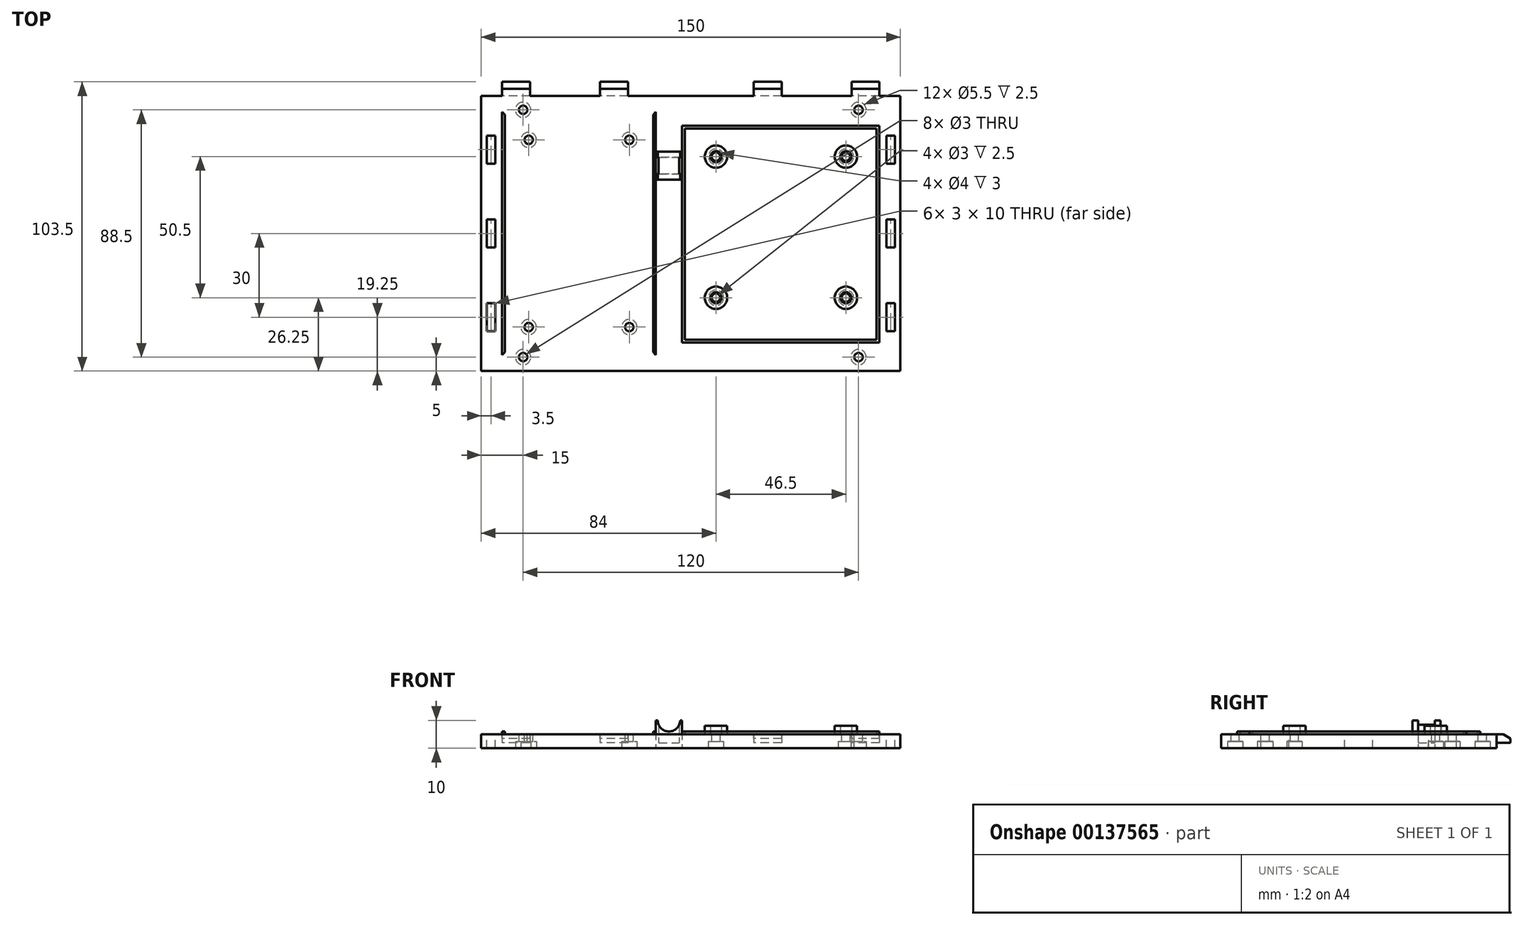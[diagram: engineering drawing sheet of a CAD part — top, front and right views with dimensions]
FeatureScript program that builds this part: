
annotation { "Feature Type Name" : "Feature", "Feature Type Description" : "" }
export const myFeature = defineFeature(function(context is Context, id is Id, definition is map)
    precondition{}
    {
        {
            var Q0;
            Q0=qCreatedBy(makeId("Top.planeOp"),FACE);
            var sketch = newSketch(context, id + "F0", { "sketchPlane" : qUnion([Q0])});
            skLineSegment(sketch, "E0.bottom", {"start": v(75, 49.25) * mm, "end": v(-75, 49.25) * mm});
            skLineSegment(sketch, "E0.top", {"start": v(75, -49.25) * mm, "end": v(-75, -49.25) * mm});
            skLineSegment(sketch, "E0.left", {"start": v(75, 49.25) * mm, "end": v(75, -49.25) * mm});
            skLineSegment(sketch, "E0.right", {"start": v(-75, 49.25) * mm, "end": v(-75, -49.25) * mm});
            skPoint(sketch, "E0.middle", {"position": v(0, 0) * mm});
            skSolve(sketch);
        }
        {
            var Q0;
            Q0=makeQuery(id+"F0.imprint","IMPRINT",FACE,{"disambiguationData":[TD([[makeQuery(id+"F0.imprint","IMPRINT",EDGE,{"derivedFrom":sQuery(id+"F0.wireOp",EDGE,"E0.bottom")}),1.0]])]});
            extrude(context, id + "F1", {"entities" : qUnion([Q0]), "depth" : 5 * mm});
        }
        {
            var Q0;
            Q0=makeQuery(id+"F1.opExtrude","CAP_FACE",FACE,{"disambiguationData":[OSD([sQuery(id+"F0.wireOp",EDGE,"E0.bottom"),sQuery(id+"F0.wireOp",EDGE,"E0.top"),sQuery(id+"F0.wireOp",EDGE,"E0.left"),sQuery(id+"F0.wireOp",EDGE,"E0.right")])],"isStart":false});
            var sketch = newSketch(context, id + "F2", { "sketchPlane" : qUnion([Q0])});
            skLineSegment(sketch, "E1.bottom", {"start": v(-62.5, 38.5) * mm, "end": v(-17.5, 38.5) * mm});
            skLineSegment(sketch, "E1.top", {"start": v(-62.5, -38.5) * mm, "end": v(-17.5, -38.5) * mm});
            skLineSegment(sketch, "E1.left", {"start": v(-62.5, 38.5) * mm, "end": v(-62.5, -38.5) * mm});
            skLineSegment(sketch, "E1.right", {"start": v(-17.5, 38.5) * mm, "end": v(-17.5, -38.5) * mm});
            skLineSegment(sketch, "E2.bottom", {"start": v(1.85, 33.5) * mm, "end": v(62.5, 33.5) * mm});
            skLineSegment(sketch, "E2.top", {"start": v(1.85, -34.05) * mm, "end": v(62.5, -34.05) * mm});
            skLineSegment(sketch, "E2.left", {"start": v(1.85, 33.5) * mm, "end": v(1.85, -34.05) * mm});
            skLineSegment(sketch, "E2.right", {"start": v(62.5, 33.5) * mm, "end": v(62.5, -34.05) * mm});
            skSolve(sketch);
        }
        {
            var Q0;
            Q0=makeQuery(id+"F2.imprint","IMPRINT",FACE,{"disambiguationData":[TD([[makeQuery(id+"F2.imprint","IMPRINT",EDGE,{"derivedFrom":sQuery(id+"F2.wireOp",EDGE,"E1.bottom")}),1.0]])]});
            var sketch = newSketch(context, id + "F3", { "sketchPlane" : qUnion([Q0])});
            skLineSegment(sketch, "E3.left", {"start": v(-66.5, 42.5) * mm, "end": v(-66.5, -42.5) * mm});
            skLineSegment(sketch, "E3.right", {"start": v(-13.5, 42.5) * mm, "end": v(-13.5, -42.5) * mm});
            skLineSegment(sketch, "E4.bottom", {"start": v(-2.15, 37.5) * mm, "end": v(66.5, 37.5) * mm});
            skLineSegment(sketch, "E4.top", {"start": v(-2.15, -38.05) * mm, "end": v(66.5, -38.05) * mm});
            skLineSegment(sketch, "E4.left", {"start": v(-2.15, 37.5) * mm, "end": v(-2.15, -38.05) * mm});
            skLineSegment(sketch, "E4.right", {"start": v(66.5, 37.5) * mm, "end": v(66.5, -38.05) * mm});
            skLineSegment(sketch, "E5.left", {"start": v(-67.5, 43.5) * mm, "end": v(-67.5, -43.5) * mm});
            skLineSegment(sketch, "E5.right", {"start": v(-12.5, 43.5) * mm, "end": v(-12.5, -43.5) * mm});
            skLineSegment(sketch, "E6.bottom", {"start": v(-3.15, 38.5) * mm, "end": v(67.5, 38.5) * mm});
            skLineSegment(sketch, "E6.top", {"start": v(-3.15, -39.05) * mm, "end": v(67.5, -39.05) * mm});
            skLineSegment(sketch, "E6.left", {"start": v(-3.15, 38.5) * mm, "end": v(-3.15, -39.05) * mm});
            skLineSegment(sketch, "E6.right", {"start": v(67.5, 38.5) * mm, "end": v(67.5, -39.05) * mm});
            skLineSegment(sketch, "E7", {"start": v(-67.5, 43.5) * mm, "end": v(-66.5, 42.5) * mm});
            skLineSegment(sketch, "E8", {"start": v(-12.5, 43.5) * mm, "end": v(-13.5, 42.5) * mm});
            skLineSegment(sketch, "E9", {"start": v(-12.5, -43.5) * mm, "end": v(-13.5, -42.5) * mm});
            skLineSegment(sketch, "E10", {"start": v(-67.5, -43.5) * mm, "end": v(-66.5, -42.5) * mm});
            skSolve(sketch);
        }
        {
            var Q0;
            Q0 = qSketchRegion(id + "F3", true);
            extrude(context, id + "F4", {"entities" : qUnion([Q0]), "operationType" : NewBodyOperationType.ADD, "depth" : 1 * mm});
        }
        {
            var Q0;
            Q0=makeQuery(id+"F2.imprint","IMPRINT",FACE,{"disambiguationData":[TD([[makeQuery(id+"F2.imprint","IMPRINT",EDGE,{"derivedFrom":sQuery(id+"F2.wireOp",EDGE,"E1.bottom")}),1.0]])]});
            var sketch = newSketch(context, id + "F5", { "sketchPlane" : qUnion([Q0])});
            skCircle(sketch, "E11", {"center": v(9, 27.5) * mm, "radius": 2 * mm});
            skCircle(sketch, "E12", {"center": v(55.5, 27.5) * mm, "radius": 2 * mm});
            skCircle(sketch, "E13", {"center": v(9, -23) * mm, "radius": 2 * mm});
            skCircle(sketch, "E14", {"center": v(55.5, -23) * mm, "radius": 2 * mm});
            skCircle(sketch, "E15", {"center": v(9, 27.5) * mm, "radius": 4 * mm});
            skCircle(sketch, "E16", {"center": v(55.5, 27.5) * mm, "radius": 4 * mm});
            skCircle(sketch, "E17", {"center": v(55.5, -23) * mm, "radius": 4 * mm});
            skCircle(sketch, "E18", {"center": v(9, -23) * mm, "radius": 4 * mm});
            skSolve(sketch);
        }
        {
            var Q0;
            Q0 = qSketchRegion(id + "F5", true);
            extrude(context, id + "F6", {"entities" : qUnion([Q0]), "operationType" : NewBodyOperationType.ADD, "depth" : 3 * mm});
        }
        {
            var Q0;
            Q0=makeQuery(id+"F2.imprint","IMPRINT",FACE,{"disambiguationData":[TD([[makeQuery(id+"F2.imprint","IMPRINT",EDGE,{"derivedFrom":sQuery(id+"F2.wireOp",EDGE,"E2.bottom")}),-1.0]])]});
            var sketch = newSketch(context, id + "F7", { "sketchPlane" : qUnion([Q0])});
            skCircle(sketch, "E19", {"center": v(9, 27.5) * mm, "radius": 1.5 * mm});
            skCircle(sketch, "E20", {"center": v(55.5, 27.5) * mm, "radius": 1.5 * mm});
            skCircle(sketch, "E21", {"center": v(9, -23) * mm, "radius": 1.5 * mm});
            skCircle(sketch, "E22", {"center": v(55.5, -23) * mm, "radius": 1.5 * mm});
            skCircle(sketch, "E23", {"center": v(-58, 33.5) * mm, "radius": 1.5 * mm});
            skCircle(sketch, "E24", {"center": v(-22, 33.5) * mm, "radius": 1.5 * mm});
            skCircle(sketch, "E25", {"center": v(-58, -33.5) * mm, "radius": 1.5 * mm});
            skCircle(sketch, "E26", {"center": v(-22, -33.5) * mm, "radius": 1.5 * mm});
            skCircle(sketch, "E27", {"center": v(-60, -44.25) * mm, "radius": 1.5 * mm});
            skCircle(sketch, "E28", {"center": v(60, -44.25) * mm, "radius": 1.5 * mm});
            skCircle(sketch, "E29", {"center": v(60, 44.25) * mm, "radius": 1.5 * mm});
            skCircle(sketch, "E30", {"center": v(-60, 44.25) * mm, "radius": 1.5 * mm});
            skSolve(sketch);
        }
        {
            var Q0;
            Q0 = qSketchRegion(id + "F7", true);
            extrude(context, id + "F8", {"entities" : qUnion([Q0]), "operationType" : NewBodyOperationType.REMOVE, "endBound" : BoundingType.SYMMETRIC, "oppositeDirection" : true, "depth" : 25 * mm});
        }
        {
            var Q0;
            Q0=makeQuery(id+"F1.opExtrude","CAP_FACE",FACE,{"disambiguationData":[OSD([sQuery(id+"F0.wireOp",EDGE,"E0.bottom"),sQuery(id+"F0.wireOp",EDGE,"E0.top"),sQuery(id+"F0.wireOp",EDGE,"E0.left"),sQuery(id+"F0.wireOp",EDGE,"E0.right")])],"isStart":true});
            var sketch = newSketch(context, id + "F9", { "sketchPlane" : qUnion([Q0])});
            skCircle(sketch, "E31", {"center": v(9, 23) * mm, "radius": 2.75 * mm});
            skCircle(sketch, "E32", {"center": v(55.5, 23) * mm, "radius": 2.75 * mm});
            skCircle(sketch, "E33", {"center": v(9, -27.5) * mm, "radius": 2.75 * mm});
            skCircle(sketch, "E34", {"center": v(55.5, -27.5) * mm, "radius": 2.75 * mm});
            skCircle(sketch, "E35", {"center": v(-22, -33.5) * mm, "radius": 2.75 * mm});
            skCircle(sketch, "E36", {"center": v(-58, -33.5) * mm, "radius": 2.75 * mm});
            skCircle(sketch, "E37", {"center": v(-22, 33.5) * mm, "radius": 2.75 * mm});
            skCircle(sketch, "E38", {"center": v(-58, 33.5) * mm, "radius": 2.75 * mm});
            skCircle(sketch, "E39", {"center": v(-60, -44.25) * mm, "radius": 2.75 * mm});
            skCircle(sketch, "E40", {"center": v(60, -44.25) * mm, "radius": 2.75 * mm});
            skCircle(sketch, "E41", {"center": v(-60, 44.25) * mm, "radius": 2.75 * mm});
            skCircle(sketch, "E42", {"center": v(60, 44.25) * mm, "radius": 2.75 * mm});
            skSolve(sketch);
        }
        {
            var Q0;
            Q0 = qSketchRegion(id + "F9", true);
            extrude(context, id + "F10", {"entities" : qUnion([Q0]), "operationType" : NewBodyOperationType.REMOVE, "oppositeDirection" : true, "depth" : 2.5 * mm});
        }
        {
            var Q0;
            Q0=makeQuery(id+"F2.imprint","IMPRINT",FACE,{"disambiguationData":[TD([[makeQuery(id+"F2.imprint","IMPRINT",EDGE,{"derivedFrom":sQuery(id+"F2.wireOp",EDGE,"E1.bottom")}),1.0]])]});
            var sketch = newSketch(context, id + "F11", { "sketchPlane" : qUnion([Q0])});
            skLineSegment(sketch, "E43.bottom", {"start": v(-73, 35) * mm, "end": v(-70, 35) * mm});
            skLineSegment(sketch, "E43.top", {"start": v(-73, 25) * mm, "end": v(-70, 25) * mm});
            skLineSegment(sketch, "E43.left", {"start": v(-73, 35) * mm, "end": v(-73, 25) * mm});
            skLineSegment(sketch, "E43.right", {"start": v(-70, 35) * mm, "end": v(-70, 25) * mm});
            skLineSegment(sketch, "E44.bottom", {"start": v(-73, 5) * mm, "end": v(-70, 5) * mm});
            skLineSegment(sketch, "E44.top", {"start": v(-73, -5) * mm, "end": v(-70, -5) * mm});
            skLineSegment(sketch, "E44.left", {"start": v(-73, 5) * mm, "end": v(-73, -5) * mm});
            skLineSegment(sketch, "E44.right", {"start": v(-70, 5) * mm, "end": v(-70, -5) * mm});
            skLineSegment(sketch, "E45.bottom", {"start": v(-73, -25) * mm, "end": v(-70, -25) * mm});
            skLineSegment(sketch, "E45.top", {"start": v(-73, -35) * mm, "end": v(-70, -35) * mm});
            skLineSegment(sketch, "E45.left", {"start": v(-73, -25) * mm, "end": v(-73, -35) * mm});
            skLineSegment(sketch, "E45.right", {"start": v(-70, -25) * mm, "end": v(-70, -35) * mm});
            skLineSegment(sketch, "E46.MirrorCS", {"start": v(73, -35) * mm, "end": v(70, -35) * mm});
            skLineSegment(sketch, "E47.MirrorCS", {"start": v(73, 35) * mm, "end": v(70, 35) * mm});
            skLineSegment(sketch, "E48.MirrorCS", {"start": v(73, -25) * mm, "end": v(70, -25) * mm});
            skLineSegment(sketch, "E49.MirrorCS", {"start": v(73, 25) * mm, "end": v(70, 25) * mm});
            skLineSegment(sketch, "E50.MirrorCS", {"start": v(73, 5) * mm, "end": v(70, 5) * mm});
            skLineSegment(sketch, "E51.MirrorCS", {"start": v(73, -5) * mm, "end": v(70, -5) * mm});
            skLineSegment(sketch, "E52.MirrorCS", {"start": v(70, -25) * mm, "end": v(70, -35) * mm});
            skLineSegment(sketch, "E53.MirrorCS", {"start": v(73, -25) * mm, "end": v(73, -35) * mm});
            skLineSegment(sketch, "E54.MirrorCS", {"start": v(73, 35) * mm, "end": v(73, 25) * mm});
            skLineSegment(sketch, "E55.MirrorCS", {"start": v(70, 35) * mm, "end": v(70, 25) * mm});
            skLineSegment(sketch, "E56.MirrorCS", {"start": v(73, 5) * mm, "end": v(73, -5) * mm});
            skLineSegment(sketch, "E57.MirrorCS", {"start": v(70, 5) * mm, "end": v(70, -5) * mm});
            skSolve(sketch);
        }
        {
            var Q0;
            Q0 = qSketchRegion(id + "F11", true);
            extrude(context, id + "F12", {"entities" : qUnion([Q0]), "operationType" : NewBodyOperationType.REMOVE, "oppositeDirection" : true, "depth" : 25 * mm});
        }
        {
            var Q0;
            Q0=makeQuery(id+"F2.imprint","IMPRINT",FACE,{"disambiguationData":[TD([[makeQuery(id+"F2.imprint","IMPRINT",EDGE,{"derivedFrom":sQuery(id+"F2.wireOp",EDGE,"E1.bottom")}),1.0]])]});
            var sketch = newSketch(context, id + "F13", { "sketchPlane" : qUnion([Q0])});
            skLineSegment(sketch, "E58.bottom", {"start": v(-12.5, 29.25) * mm, "end": v(-3.15, 29.25) * mm});
            skLineSegment(sketch, "E58.top", {"start": v(-12.5, 19.25) * mm, "end": v(-3.15, 19.25) * mm});
            skLineSegment(sketch, "E58.left", {"start": v(-12.5, 29.25) * mm, "end": v(-12.5, 19.25) * mm});
            skLineSegment(sketch, "E58.right", {"start": v(-3.15, 29.25) * mm, "end": v(-3.15, 19.25) * mm});
            skLineSegment(sketch, "E59.bottom", {"start": v(-12.5, 27.25) * mm, "end": v(-11.5, 27.25) * mm});
            skLineSegment(sketch, "E59.top", {"start": v(-12.5, 21.25) * mm, "end": v(-11.5, 21.25) * mm});
            skLineSegment(sketch, "E59.left", {"start": v(-12.5, 27.25) * mm, "end": v(-12.5, 21.25) * mm});
            skLineSegment(sketch, "E59.right", {"start": v(-11.5, 27.25) * mm, "end": v(-11.5, 21.25) * mm});
            skLineSegment(sketch, "E60", {"start": v(-7.82, 29.25) * mm, "end": v(-7.82, 19.25) * mm});
            skLineSegment(sketch, "E61.MirrorCS", {"start": v(-4.15, 27.25) * mm, "end": v(-4.15, 21.25) * mm});
            skLineSegment(sketch, "E62.MirrorCS", {"start": v(-3.15, 27.25) * mm, "end": v(-3.15, 21.25) * mm});
            skLineSegment(sketch, "E63.MirrorCS", {"start": v(-3.15, 21.25) * mm, "end": v(-4.15, 21.25) * mm});
            skLineSegment(sketch, "E64.MirrorCS", {"start": v(-3.15, 27.25) * mm, "end": v(-4.15, 27.25) * mm});
            skSolve(sketch);
        }
        {
            var Q0;
            {var subQ4=sQuery(id+"F13.wireOp",EDGE,"E59.bottom");Q0=makeQuery(id+"F13.imprint","IMPRINT",FACE,{"disambiguationData":[TD([[makeQuery(id+"F13.imprint","IMPRINT",EDGE,{"derivedFrom":subQ4}),1.0]])]});}
            var Q1;
            {var subQ0=sQuery(id+"F13.wireOp",EDGE,"E60");Q1=makeQuery(id+"F13.imprint","IMPRINT",FACE,{"disambiguationData":[TD([[makeQuery(id+"F13.imprint","IMPRINT",EDGE,{"derivedFrom":subQ0}),1.0]])]});}
            extrude(context, id + "F14", {"entities" : qUnion([Q0, Q1]), "operationType" : NewBodyOperationType.ADD, "depth" : 5 * mm});
        }
        {
            var Q0;
            Q0=makeQuery(id+"F14.opExtrude","SWEPT_FACE",FACE,{"disambiguationData":[OSD([sQuery(id+"F13.wireOp",EDGE,"E58.top")])]});
            var sketch = newSketch(context, id + "F15", { "sketchPlane" : qUnion([Q0])});
            skCircle(sketch, "E65", {"center": v(-7.82, 10) * mm, "radius": 4 * mm});
            skSolve(sketch);
        }
        {
            var Q0;
            Q0 = qSketchRegion(id + "F15", true);
            extrude(context, id + "F16", {"entities" : qUnion([Q0]), "operationType" : NewBodyOperationType.REMOVE, "oppositeDirection" : true, "depth" : 25 * mm});
        }
        {
            var Q0;
            Q0=makeQuery(id+"F13.imprint","IMPRINT",FACE,{"disambiguationData":[TD([[makeQuery(id+"F13.imprint","IMPRINT",EDGE,{"derivedFrom":sQuery(id+"F13.wireOp",EDGE,"E59.bottom")}),-1.0]])]});
            var Q1;
            Q1=makeQuery(id+"F13.imprint","IMPRINT",FACE,{"disambiguationData":[TD([[makeQuery(id+"F13.imprint","IMPRINT",EDGE,{"derivedFrom":sQuery(id+"F13.wireOp",EDGE,"E61.MirrorCS")}),1.0]])]});
            extrude(context, id + "F17", {"entities" : qUnion([Q0, Q1]), "operationType" : NewBodyOperationType.REMOVE, "oppositeDirection" : true, "depth" : 25 * mm});
        }
        {
            var Q0;
            Q0=makeQuery(id+"F1.opExtrude","CAP_FACE",FACE,{"disambiguationData":[OSD([sQuery(id+"F0.wireOp",EDGE,"E0.bottom"),sQuery(id+"F0.wireOp",EDGE,"E0.top"),sQuery(id+"F0.wireOp",EDGE,"E0.left"),sQuery(id+"F0.wireOp",EDGE,"E0.right")])],"isStart":true});
            var sketch = newSketch(context, id + "F18", { "sketchPlane" : qUnion([Q0])});
            skLineSegment(sketch, "E66.bottom", {"start": v(-12.5, -27.25) * mm, "end": v(-3.15, -27.25) * mm});
            skLineSegment(sketch, "E66.top", {"start": v(-12.5, -21.25) * mm, "end": v(-3.15, -21.25) * mm});
            skLineSegment(sketch, "E66.left", {"start": v(-12.5, -27.25) * mm, "end": v(-12.5, -21.25) * mm});
            skLineSegment(sketch, "E66.right", {"start": v(-3.15, -27.25) * mm, "end": v(-3.15, -21.25) * mm});
            skSolve(sketch);
        }
        {
            var Q0;
            Q0 = qSketchRegion(id + "F18", true);
            extrude(context, id + "F19", {"entities" : qUnion([Q0]), "operationType" : NewBodyOperationType.REMOVE, "oppositeDirection" : true, "depth" : 2 * mm});
        }
        {
            var Q0;
            Q0=makeQuery(id+"F1.opExtrude","SWEPT_FACE",FACE,{"disambiguationData":[OSD([sQuery(id+"F0.wireOp",EDGE,"E0.bottom")])]});
            var sketch = newSketch(context, id + "F20", { "sketchPlane" : qUnion([Q0])});
            skLineSegment(sketch, "E67.bottom", {"start": v(-67.5, 5) * mm, "end": v(-57.5, 5) * mm});
            skLineSegment(sketch, "E67.top", {"start": v(-67.5, 2) * mm, "end": v(-57.5, 2) * mm});
            skLineSegment(sketch, "E67.left", {"start": v(-67.5, 5) * mm, "end": v(-67.5, 2) * mm});
            skLineSegment(sketch, "E67.right", {"start": v(-57.5, 5) * mm, "end": v(-57.5, 2) * mm});
            skLineSegment(sketch, "E68.bottom", {"start": v(-32.5, 5) * mm, "end": v(-22.5, 5) * mm});
            skLineSegment(sketch, "E68.top", {"start": v(-32.5, 2) * mm, "end": v(-22.5, 2) * mm});
            skLineSegment(sketch, "E68.left", {"start": v(-32.5, 5) * mm, "end": v(-32.5, 2) * mm});
            skLineSegment(sketch, "E68.right", {"start": v(-22.5, 5) * mm, "end": v(-22.5, 2) * mm});
            skLineSegment(sketch, "E69.bottom", {"start": v(22.5, 5) * mm, "end": v(32.5, 5) * mm});
            skLineSegment(sketch, "E69.top", {"start": v(22.5, 2) * mm, "end": v(32.5, 2) * mm});
            skLineSegment(sketch, "E69.left", {"start": v(22.5, 5) * mm, "end": v(22.5, 2) * mm});
            skLineSegment(sketch, "E69.right", {"start": v(32.5, 5) * mm, "end": v(32.5, 2) * mm});
            skLineSegment(sketch, "E70.bottom", {"start": v(57.5, 5) * mm, "end": v(67.5, 5) * mm});
            skLineSegment(sketch, "E70.top", {"start": v(57.5, 2) * mm, "end": v(67.5, 2) * mm});
            skLineSegment(sketch, "E70.left", {"start": v(57.5, 5) * mm, "end": v(57.5, 2) * mm});
            skLineSegment(sketch, "E70.right", {"start": v(67.5, 5) * mm, "end": v(67.5, 2) * mm});
            skSolve(sketch);
        }
        {
            var Q0;
            Q0 = qSketchRegion(id + "F20", true);
            extrude(context, id + "F21", {"entities" : qUnion([Q0]), "operationType" : NewBodyOperationType.ADD, "depth" : 5 * mm});
        }
        {
            var Q0;
            Q0=makeQuery(id+"F21.opExtrude","SWEPT_FACE",FACE,{"disambiguationData":[OSD([sQuery(id+"F20.wireOp",EDGE,"E70.right")])]});
            var sketch = newSketch(context, id + "F22", { "sketchPlane" : qUnion([Q0])});
            skLineSegment(sketch, "E71", {"start": v(-54.25, 3.5) * mm, "end": v(-51.75, 5) * mm});
            skSolve(sketch);
        }
        {
            var Q0;
            {var subQ0=sQuery(id+"F22.wireOp",EDGE,"E71");Q0=makeQuery(id+"F22.imprint","IMPRINT",FACE,{"disambiguationData":[TD([[makeQuery(id+"F22.imprint","IMPRINT",EDGE,{"derivedFrom":subQ0}),1.0]])]});}
            extrude(context, id + "F23", {"entities" : qUnion([Q0]), "operationType" : NewBodyOperationType.REMOVE, "oppositeDirection" : true, "depth" : 200 * mm});
        }
    });
